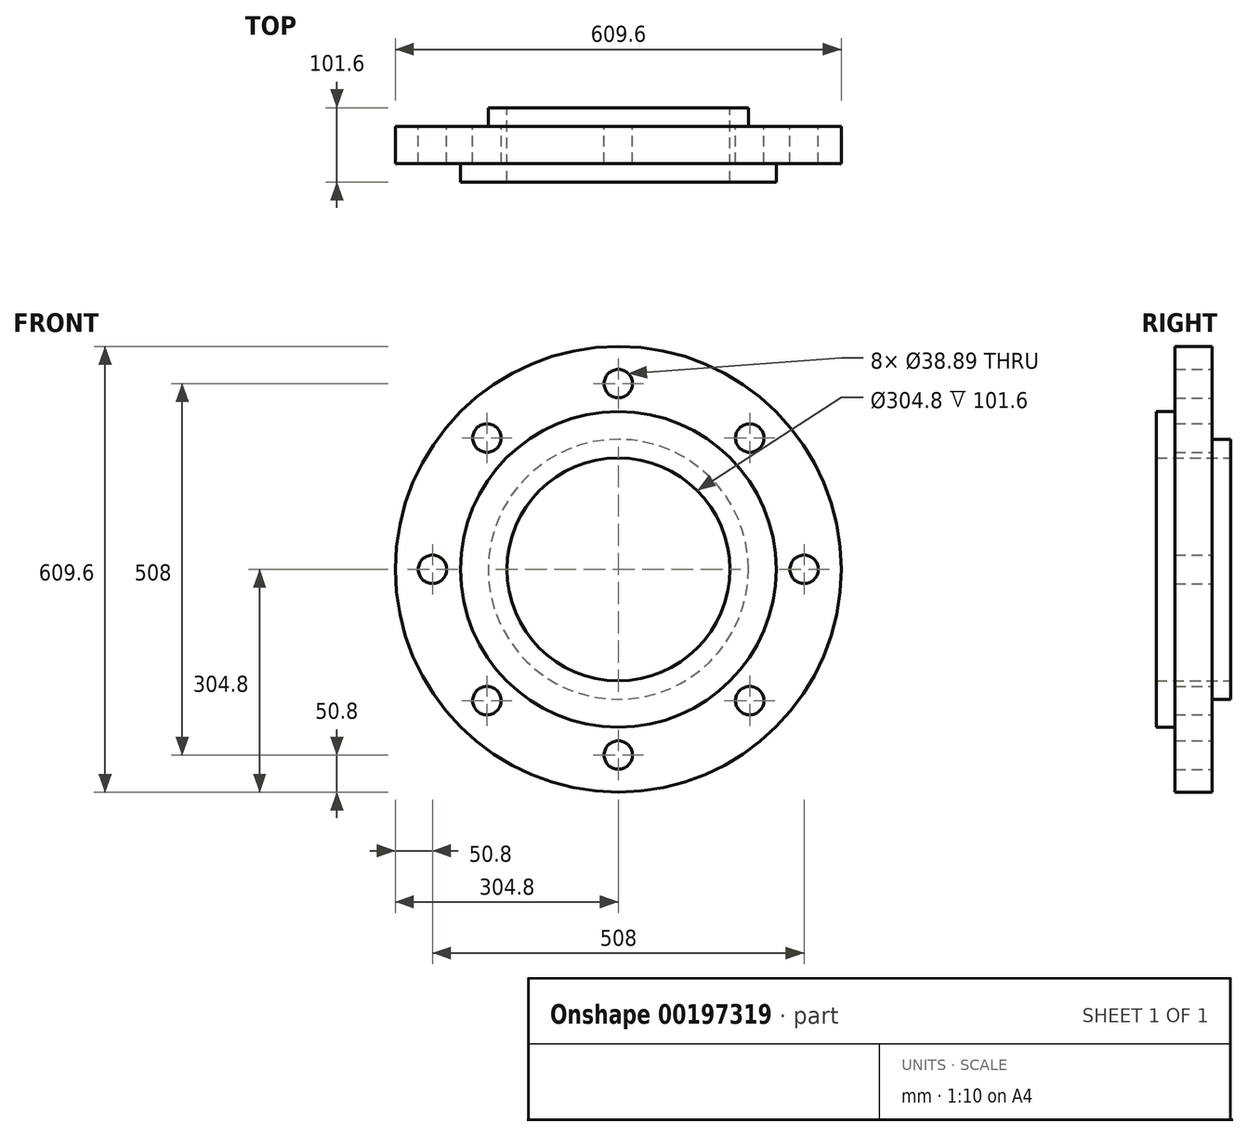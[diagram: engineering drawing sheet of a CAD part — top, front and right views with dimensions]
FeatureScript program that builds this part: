
annotation { "Feature Type Name" : "Feature", "Feature Type Description" : "" }
export const myFeature = defineFeature(function(context is Context, id is Id, definition is map)
    precondition{}
    {
        {
            var Q0;
            Q0=qCreatedBy(makeId("Front.planeOp"),FACE);
            var sketch = newSketch(context, id + "F0", { "sketchPlane" : qUnion([Q0])});
            skCircle(sketch, "E0", {"center": v(0, 0) * mm, "radius": 304.8 * mm});
            skCircle(sketch, "E1", {"center": v(0, 254) * mm, "radius": 19.44 * mm});
            skCircle(sketch, "E2.1.0", {"center": v(-179.6, 179.6) * mm, "radius": 19.44 * mm});
            skCircle(sketch, "E2.2.0", {"center": v(-254, 0) * mm, "radius": 19.44 * mm});
            skCircle(sketch, "E2.3.0", {"center": v(-179.6, -179.6) * mm, "radius": 19.44 * mm});
            skCircle(sketch, "E2.4.0", {"center": v(0, -254) * mm, "radius": 19.44 * mm});
            skCircle(sketch, "E2.5.0", {"center": v(179.6, -179.6) * mm, "radius": 19.44 * mm});
            skCircle(sketch, "E2.6.0", {"center": v(254, 0) * mm, "radius": 19.44 * mm});
            skCircle(sketch, "E2.7.0", {"center": v(179.6, 179.6) * mm, "radius": 19.44 * mm});
            skCircle(sketch, "E3", {"center": v(0, 0) * mm, "radius": 152.4 * mm});
            skSolve(sketch);
        }
        {
            var Q0;
            Q0=makeQuery(id+"F0.imprint","IMPRINT",FACE,{"disambiguationData":[TD([[makeQuery(id+"F0.imprint","IMPRINT",EDGE,{"derivedFrom":sQuery(id+"F0.wireOp",EDGE,"E0")}),1.0]])]});
            extrude(context, id + "F1", {"entities" : qUnion([Q0]), "endBound" : BoundingType.SYMMETRIC, "depth" : 50.8 * mm});
        }
        {
            var Q0;
            Q0=makeQuery(id+"F1.opExtrude","CAP_FACE",FACE,{"disambiguationData":[OSD([sQuery(id+"F0.wireOp",EDGE,"E0"),sQuery(id+"F0.wireOp",EDGE,"E1"),sQuery(id+"F0.wireOp",EDGE,"E2.1.0"),sQuery(id+"F0.wireOp",EDGE,"E2.2.0"),sQuery(id+"F0.wireOp",EDGE,"E2.3.0"),sQuery(id+"F0.wireOp",EDGE,"E2.4.0"),sQuery(id+"F0.wireOp",EDGE,"E2.5.0"),sQuery(id+"F0.wireOp",EDGE,"E2.6.0"),sQuery(id+"F0.wireOp",EDGE,"E2.7.0"),sQuery(id+"F0.wireOp",EDGE,"E3")])],"isStart":false});
            var sketch = newSketch(context, id + "F2", { "sketchPlane" : qUnion([Q0])});
            skCircle(sketch, "E4", {"center": v(0, 0) * mm, "radius": 215.9 * mm});
            skCircle(sketch, "E5.0", {"center": v(0, 0) * mm, "radius": 152.4 * mm});
            skSolve(sketch);
        }
        {
            var Q0;
            Q0=makeQuery(id+"F2.imprint","IMPRINT",FACE,{"disambiguationData":[TD([[makeQuery(id+"F2.imprint","IMPRINT",EDGE,{"derivedFrom":sQuery(id+"F2.wireOp",EDGE,"E4")}),1.0]])]});
            extrude(context, id + "F3", {"entities" : qUnion([Q0]), "operationType" : NewBodyOperationType.ADD, "depth" : 25.4 * mm});
        }
        {
            var Q0;
            Q0=makeQuery(id+"F1.opExtrude","CAP_FACE",FACE,{"disambiguationData":[OSD([sQuery(id+"F0.wireOp",EDGE,"E0"),sQuery(id+"F0.wireOp",EDGE,"E1"),sQuery(id+"F0.wireOp",EDGE,"E2.1.0"),sQuery(id+"F0.wireOp",EDGE,"E2.2.0"),sQuery(id+"F0.wireOp",EDGE,"E2.3.0"),sQuery(id+"F0.wireOp",EDGE,"E2.4.0"),sQuery(id+"F0.wireOp",EDGE,"E2.5.0"),sQuery(id+"F0.wireOp",EDGE,"E2.6.0"),sQuery(id+"F0.wireOp",EDGE,"E2.7.0"),sQuery(id+"F0.wireOp",EDGE,"E3")])],"isStart":true});
            var sketch = newSketch(context, id + "F4", { "sketchPlane" : qUnion([Q0])});
            skCircle(sketch, "E6", {"center": v(0, 0) * mm, "radius": 177.8 * mm});
            skCircle(sketch, "E7.0", {"center": v(0, 0) * mm, "radius": 152.4 * mm});
            skSolve(sketch);
        }
        {
            var Q0;
            Q0=makeQuery(id+"F4.imprint","IMPRINT",FACE,{"disambiguationData":[TD([[makeQuery(id+"F4.imprint","IMPRINT",EDGE,{"derivedFrom":sQuery(id+"F4.wireOp",EDGE,"E6")}),1.0]])]});
            extrude(context, id + "F5", {"entities" : qUnion([Q0]), "operationType" : NewBodyOperationType.ADD, "depth" : 25.4 * mm});
        }
    });
